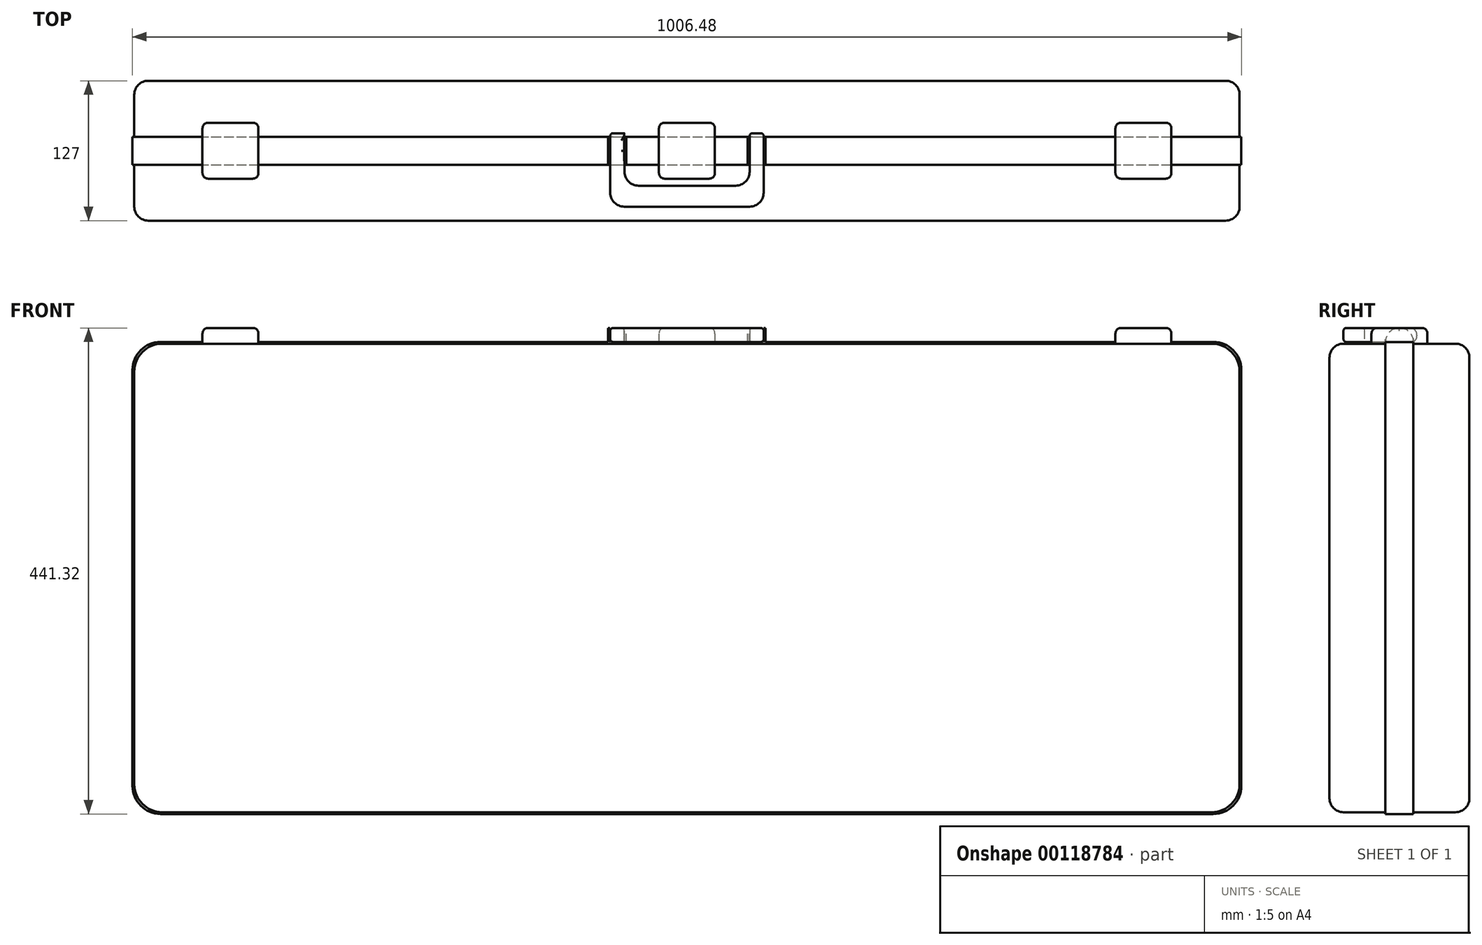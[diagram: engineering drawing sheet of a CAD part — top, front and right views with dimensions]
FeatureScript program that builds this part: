
annotation { "Feature Type Name" : "Feature", "Feature Type Description" : "" }
export const myFeature = defineFeature(function(context is Context, id is Id, definition is map)
    precondition{}
    {
        {
            var Q0;
            Q0=qCreatedBy(makeId("Front.planeOp"),FACE);
            var sketch = newSketch(context, id + "F0", { "sketchPlane" : qUnion([Q0])});
            skLineSegment(sketch, "E0.bottom", {"start": v(-501.65, 212.73) * mm, "end": v(501.65, 212.73) * mm});
            skLineSegment(sketch, "E0.top", {"start": v(-501.65, -212.73) * mm, "end": v(501.65, -212.73) * mm});
            skLineSegment(sketch, "E0.left", {"start": v(-501.65, 212.73) * mm, "end": v(-501.65, -212.73) * mm});
            skLineSegment(sketch, "E0.right", {"start": v(501.65, 212.73) * mm, "end": v(501.65, -212.73) * mm});
            skPoint(sketch, "E0.middle", {"position": v(0, 0) * mm});
            skSolve(sketch);
        }
        {
            var Q0;
            Q0 = qSketchRegion(id + "F0", true);
            extrude(context, id + "F1", {"entities" : qUnion([Q0]), "depth" : 63.5 * mm, "hasSecondDirection" : true, "secondDirectionOppositeDirection" : true, "secondDirectionDepth" : 63.5 * mm});
        }
        {
            var Q0;
            Q0=qCreatedBy(makeId("Front.planeOp"),FACE);
            var sketch = newSketch(context, id + "F2", { "sketchPlane" : qUnion([Q0])});
            skLineSegment(sketch, "E1.bottom", {"start": v(-503.24, 214.31) * mm, "end": v(503.24, 214.31) * mm});
            skLineSegment(sketch, "E1.top", {"start": v(-503.24, -214.31) * mm, "end": v(503.24, -214.31) * mm});
            skLineSegment(sketch, "E1.left", {"start": v(-503.24, 214.31) * mm, "end": v(-503.24, -214.31) * mm});
            skLineSegment(sketch, "E1.right", {"start": v(503.24, 214.31) * mm, "end": v(503.24, -214.31) * mm});
            skPoint(sketch, "E1.middle", {"position": v(0, 0) * mm});
            skSolve(sketch);
        }
        {
            var Q0;
            Q0 = qSketchRegion(id + "F2", true);
            extrude(context, id + "F3", {"entities" : qUnion([Q0]), "operationType" : NewBodyOperationType.ADD, "depth" : 12.7 * mm, "hasSecondDirection" : true, "secondDirectionOppositeDirection" : true, "secondDirectionDepth" : 12.7 * mm});
        }
        {
            var Q0;
            {var subQ0=sQuery(id+"F0.wireOp",EDGE,"E0.bottom");var subQ1=sQuery(id+"F0.wireOp",EDGE,"E0.right");Q0=makeQuery(id+"F3.boolean.opBoolean","SPLIT",EDGE,{"disambiguationData":[TD([makeQuery(id+"F1.opExtrude","CAP_FACE",FACE,{"disambiguationData":[OSD([subQ0,sQuery(id+"F0.wireOp",EDGE,"E0.top"),sQuery(id+"F0.wireOp",EDGE,"E0.left"),subQ1])],"isStart":false})])],"derivedFrom":makeQuery(id+"F1.opExtrude","SWEPT_EDGE",EDGE,{"disambiguationData":[OSD([subQ0,subQ1])]})});}
            var Q1;
            {var subQ0=sQuery(id+"F0.wireOp",EDGE,"E0.bottom");var subQ1=sQuery(id+"F0.wireOp",EDGE,"E0.right");Q1=makeQuery(id+"F3.boolean.opBoolean","SPLIT",EDGE,{"disambiguationData":[TD([makeQuery(id+"F1.opExtrude","CAP_FACE",FACE,{"disambiguationData":[OSD([subQ0,sQuery(id+"F0.wireOp",EDGE,"E0.top"),sQuery(id+"F0.wireOp",EDGE,"E0.left"),subQ1])],"isStart":true})])],"derivedFrom":makeQuery(id+"F1.opExtrude","SWEPT_EDGE",EDGE,{"disambiguationData":[OSD([subQ0,subQ1])]})});}
            var Q2;
            Q2=makeQuery(id+"F3.opExtrude","SWEPT_EDGE",EDGE,{"disambiguationData":[OSD([sQuery(id+"F2.wireOp",EDGE,"E1.bottom"),sQuery(id+"F2.wireOp",EDGE,"E1.right")])]});
            var Q3;
            {var subQ0=sQuery(id+"F0.wireOp",EDGE,"E0.right");var subQ1=sQuery(id+"F0.wireOp",EDGE,"E0.top");Q3=makeQuery(id+"F3.boolean.opBoolean","SPLIT",EDGE,{"disambiguationData":[TD([makeQuery(id+"F1.opExtrude","CAP_FACE",FACE,{"disambiguationData":[OSD([sQuery(id+"F0.wireOp",EDGE,"E0.bottom"),subQ1,sQuery(id+"F0.wireOp",EDGE,"E0.left"),subQ0])],"isStart":false})])],"derivedFrom":makeQuery(id+"F1.opExtrude","SWEPT_EDGE",EDGE,{"disambiguationData":[OSD([subQ1,subQ0])]})});}
            var Q4;
            Q4=makeQuery(id+"F3.opExtrude","SWEPT_EDGE",EDGE,{"disambiguationData":[OSD([sQuery(id+"F2.wireOp",EDGE,"E1.top"),sQuery(id+"F2.wireOp",EDGE,"E1.right")])]});
            var Q5;
            {var subQ0=sQuery(id+"F0.wireOp",EDGE,"E0.right");var subQ1=sQuery(id+"F0.wireOp",EDGE,"E0.top");Q5=makeQuery(id+"F3.boolean.opBoolean","SPLIT",EDGE,{"disambiguationData":[TD([makeQuery(id+"F1.opExtrude","CAP_FACE",FACE,{"disambiguationData":[OSD([sQuery(id+"F0.wireOp",EDGE,"E0.bottom"),subQ1,sQuery(id+"F0.wireOp",EDGE,"E0.left"),subQ0])],"isStart":true})])],"derivedFrom":makeQuery(id+"F1.opExtrude","SWEPT_EDGE",EDGE,{"disambiguationData":[OSD([subQ1,subQ0])]})});}
            var Q6;
            Q6=makeQuery(id+"F3.opExtrude","SWEPT_EDGE",EDGE,{"disambiguationData":[OSD([sQuery(id+"F2.wireOp",EDGE,"E1.bottom"),sQuery(id+"F2.wireOp",EDGE,"E1.left")])]});
            var Q7;
            {var subQ0=sQuery(id+"F0.wireOp",EDGE,"E0.bottom");var subQ1=sQuery(id+"F0.wireOp",EDGE,"E0.left");Q7=makeQuery(id+"F3.boolean.opBoolean","SPLIT",EDGE,{"disambiguationData":[TD([makeQuery(id+"F1.opExtrude","CAP_FACE",FACE,{"disambiguationData":[OSD([subQ0,sQuery(id+"F0.wireOp",EDGE,"E0.top"),subQ1,sQuery(id+"F0.wireOp",EDGE,"E0.right")])],"isStart":false})])],"derivedFrom":makeQuery(id+"F1.opExtrude","SWEPT_EDGE",EDGE,{"disambiguationData":[OSD([subQ0,subQ1])]})});}
            var Q8;
            {var subQ0=sQuery(id+"F0.wireOp",EDGE,"E0.bottom");var subQ1=sQuery(id+"F0.wireOp",EDGE,"E0.left");Q8=makeQuery(id+"F3.boolean.opBoolean","SPLIT",EDGE,{"disambiguationData":[TD([makeQuery(id+"F1.opExtrude","CAP_FACE",FACE,{"disambiguationData":[OSD([subQ0,sQuery(id+"F0.wireOp",EDGE,"E0.top"),subQ1,sQuery(id+"F0.wireOp",EDGE,"E0.right")])],"isStart":true})])],"derivedFrom":makeQuery(id+"F1.opExtrude","SWEPT_EDGE",EDGE,{"disambiguationData":[OSD([subQ0,subQ1])]})});}
            var Q9;
            {var subQ0=sQuery(id+"F0.wireOp",EDGE,"E0.left");var subQ1=sQuery(id+"F0.wireOp",EDGE,"E0.top");Q9=makeQuery(id+"F3.boolean.opBoolean","SPLIT",EDGE,{"disambiguationData":[TD([makeQuery(id+"F1.opExtrude","CAP_FACE",FACE,{"disambiguationData":[OSD([sQuery(id+"F0.wireOp",EDGE,"E0.bottom"),subQ1,subQ0,sQuery(id+"F0.wireOp",EDGE,"E0.right")])],"isStart":false})])],"derivedFrom":makeQuery(id+"F1.opExtrude","SWEPT_EDGE",EDGE,{"disambiguationData":[OSD([subQ1,subQ0])]})});}
            var Q10;
            Q10=makeQuery(id+"F3.opExtrude","SWEPT_EDGE",EDGE,{"disambiguationData":[OSD([sQuery(id+"F2.wireOp",EDGE,"E1.top"),sQuery(id+"F2.wireOp",EDGE,"E1.left")])]});
            var Q11;
            {var subQ0=sQuery(id+"F0.wireOp",EDGE,"E0.left");var subQ1=sQuery(id+"F0.wireOp",EDGE,"E0.top");Q11=makeQuery(id+"F3.boolean.opBoolean","SPLIT",EDGE,{"disambiguationData":[TD([makeQuery(id+"F1.opExtrude","CAP_FACE",FACE,{"disambiguationData":[OSD([sQuery(id+"F0.wireOp",EDGE,"E0.bottom"),subQ1,subQ0,sQuery(id+"F0.wireOp",EDGE,"E0.right")])],"isStart":true})])],"derivedFrom":makeQuery(id+"F1.opExtrude","SWEPT_EDGE",EDGE,{"disambiguationData":[OSD([subQ1,subQ0])]})});}
            fillet(context, id + "F4", {"entities" : qUnion([Q0, Q1, Q2, Q3, Q4, Q5, Q6, Q7, Q8, Q9, Q10, Q11]), "radius" : 25.4 * mm, "tangentPropagation" : true, "allowEdgeOverflow" : false});
        }
        {
            var Q0;
            Q0=makeQuery(id+"F1.opExtrude","CAP_EDGE",EDGE,{"disambiguationData":[OSD([sQuery(id+"F0.wireOp",EDGE,"E0.bottom")])],"isStart":false});
            var Q1;
            Q1=makeQuery(id+"F1.opExtrude","CAP_EDGE",EDGE,{"disambiguationData":[OSD([sQuery(id+"F0.wireOp",EDGE,"E0.bottom")])],"isStart":true});
            fillet(context, id + "F5", {"entities" : qUnion([Q0, Q1]), "radius" : 12.7 * mm, "tangentPropagation" : true, "allowEdgeOverflow" : false});
        }
        {
            var Q0;
            Q0=makeQuery(id+"F3.opExtrude","SWEPT_FACE",FACE,{"disambiguationData":[OSD([sQuery(id+"F2.wireOp",EDGE,"E1.bottom")])]});
            var sketch = newSketch(context, id + "F6", { "sketchPlane" : qUnion([Q0])});
            skLineSegment(sketch, "E2", {"start": v(-477.84, 12.7) * mm, "end": v(-439.74, 12.7) * mm, "construction": true});
            skLineSegment(sketch, "E3", {"start": v(-439.74, 12.7) * mm, "end": v(-439.74, 0) * mm, "construction": true});
            skLineSegment(sketch, "E4", {"start": v(-439.74, 12.7) * mm, "end": v(-439.74, 25.4) * mm, "construction": true});
            skLineSegment(sketch, "E5.bottom", {"start": v(-439.74, 25.4) * mm, "end": v(-388.94, 25.4) * mm});
            skLineSegment(sketch, "E5.top", {"start": v(-439.74, -25.4) * mm, "end": v(-388.94, -25.4) * mm});
            skLineSegment(sketch, "E5.left", {"start": v(-439.74, 25.4) * mm, "end": v(-439.74, -25.4) * mm});
            skLineSegment(sketch, "E5.right", {"start": v(-388.94, 25.4) * mm, "end": v(-388.94, -25.4) * mm});
            skLineSegment(sketch, "E6", {"start": v(477.84, 0) * mm, "end": v(439.74, 0) * mm, "construction": true});
            skLineSegment(sketch, "E7", {"start": v(439.74, 0) * mm, "end": v(439.74, 25.4) * mm, "construction": true});
            skLineSegment(sketch, "E8.bottom", {"start": v(439.74, 25.4) * mm, "end": v(388.94, 25.4) * mm});
            skLineSegment(sketch, "E8.top", {"start": v(439.74, -25.4) * mm, "end": v(388.94, -25.4) * mm});
            skLineSegment(sketch, "E8.left", {"start": v(439.74, 25.4) * mm, "end": v(439.74, -25.4) * mm});
            skLineSegment(sketch, "E8.right", {"start": v(388.94, 25.4) * mm, "end": v(388.94, -25.4) * mm});
            skLineSegment(sketch, "E9.bottom", {"start": v(25.4, -25.4) * mm, "end": v(-25.4, -25.4) * mm});
            skLineSegment(sketch, "E9.top", {"start": v(25.4, 25.4) * mm, "end": v(-25.4, 25.4) * mm});
            skLineSegment(sketch, "E9.left", {"start": v(25.4, -25.4) * mm, "end": v(25.4, 25.4) * mm});
            skLineSegment(sketch, "E9.right", {"start": v(-25.4, -25.4) * mm, "end": v(-25.4, 25.4) * mm});
            skPoint(sketch, "E9.middle", {"position": v(0, 0) * mm});
            skSolve(sketch);
        }
        {
            var Q0;
            Q0 = qSketchRegion(id + "F6", true);
            extrude(context, id + "F7", {"entities" : qUnion([Q0]), "operationType" : NewBodyOperationType.ADD, "depth" : 12.7 * mm, "hasSecondDirection" : true, "secondDirectionOppositeDirection" : true, "secondDirectionDepth" : 25.4 * mm});
        }
        {
            var Q0;
            Q0=makeQuery(id+"F7.opExtrude","SWEPT_EDGE",EDGE,{"disambiguationData":[OSD([sQuery(id+"F6.wireOp",EDGE,"E9.bottom"),sQuery(id+"F6.wireOp",EDGE,"E9.left")])]});
            var Q1;
            Q1=makeQuery(id+"F7.opExtrude","SWEPT_EDGE",EDGE,{"disambiguationData":[OSD([sQuery(id+"F6.wireOp",EDGE,"E9.bottom"),sQuery(id+"F6.wireOp",EDGE,"E9.right")])]});
            var Q2;
            Q2=makeQuery(id+"F7.opExtrude","SWEPT_EDGE",EDGE,{"disambiguationData":[OSD([sQuery(id+"F6.wireOp",EDGE,"E9.top"),sQuery(id+"F6.wireOp",EDGE,"E9.right")])]});
            var Q3;
            Q3=makeQuery(id+"F7.opExtrude","SWEPT_EDGE",EDGE,{"disambiguationData":[OSD([sQuery(id+"F6.wireOp",EDGE,"E9.top"),sQuery(id+"F6.wireOp",EDGE,"E9.left")])]});
            var Q4;
            Q4=makeQuery(id+"F7.opExtrude","SWEPT_EDGE",EDGE,{"disambiguationData":[OSD([sQuery(id+"F6.wireOp",EDGE,"E5.bottom"),sQuery(id+"F6.wireOp",EDGE,"E5.right")])]});
            var Q5;
            Q5=makeQuery(id+"F7.opExtrude","SWEPT_EDGE",EDGE,{"disambiguationData":[OSD([sQuery(id+"F6.wireOp",EDGE,"E5.bottom"),sQuery(id+"F6.wireOp",EDGE,"E5.left")])]});
            var Q6;
            Q6=makeQuery(id+"F7.opExtrude","SWEPT_EDGE",EDGE,{"disambiguationData":[OSD([sQuery(id+"F6.wireOp",EDGE,"E5.top"),sQuery(id+"F6.wireOp",EDGE,"E5.right")])]});
            var Q7;
            Q7=makeQuery(id+"F7.opExtrude","SWEPT_EDGE",EDGE,{"disambiguationData":[OSD([sQuery(id+"F6.wireOp",EDGE,"E5.top"),sQuery(id+"F6.wireOp",EDGE,"E5.left")])]});
            var Q8;
            Q8=makeQuery(id+"F7.opExtrude","SWEPT_EDGE",EDGE,{"disambiguationData":[OSD([sQuery(id+"F6.wireOp",EDGE,"E8.top"),sQuery(id+"F6.wireOp",EDGE,"E8.left")])]});
            var Q9;
            Q9=makeQuery(id+"F7.opExtrude","SWEPT_EDGE",EDGE,{"disambiguationData":[OSD([sQuery(id+"F6.wireOp",EDGE,"E8.top"),sQuery(id+"F6.wireOp",EDGE,"E8.right")])]});
            var Q10;
            Q10=makeQuery(id+"F7.opExtrude","SWEPT_EDGE",EDGE,{"disambiguationData":[OSD([sQuery(id+"F6.wireOp",EDGE,"E8.bottom"),sQuery(id+"F6.wireOp",EDGE,"E8.right")])]});
            var Q11;
            Q11=makeQuery(id+"F7.opExtrude","SWEPT_EDGE",EDGE,{"disambiguationData":[OSD([sQuery(id+"F6.wireOp",EDGE,"E8.bottom"),sQuery(id+"F6.wireOp",EDGE,"E8.left")])]});
            var Q12;
            Q12=makeQuery(id+"F7.opExtrude","CAP_FACE",FACE,{"disambiguationData":[OSD([sQuery(id+"F6.wireOp",EDGE,"E9.bottom"),sQuery(id+"F6.wireOp",EDGE,"E9.top"),sQuery(id+"F6.wireOp",EDGE,"E9.left"),sQuery(id+"F6.wireOp",EDGE,"E9.right")])],"isStart":false});
            var Q13;
            Q13=makeQuery(id+"F7.opExtrude","CAP_FACE",FACE,{"disambiguationData":[OSD([sQuery(id+"F6.wireOp",EDGE,"E8.bottom"),sQuery(id+"F6.wireOp",EDGE,"E8.top"),sQuery(id+"F6.wireOp",EDGE,"E8.left"),sQuery(id+"F6.wireOp",EDGE,"E8.right")])],"isStart":false});
            var Q14;
            Q14=makeQuery(id+"F7.opExtrude","CAP_EDGE",EDGE,{"disambiguationData":[OSD([sQuery(id+"F6.wireOp",EDGE,"E5.left")])],"isStart":false});
            var Q15;
            Q15=makeQuery(id+"F7.opExtrude","CAP_FACE",FACE,{"disambiguationData":[OSD([sQuery(id+"F6.wireOp",EDGE,"E5.bottom"),sQuery(id+"F6.wireOp",EDGE,"E5.top"),sQuery(id+"F6.wireOp",EDGE,"E5.left"),sQuery(id+"F6.wireOp",EDGE,"E5.right")])],"isStart":false});
            fillet(context, id + "F8", {"entities" : qUnion([Q0, Q1, Q2, Q3, Q4, Q5, Q6, Q7, Q8, Q9, Q10, Q11, Q12, Q13, Q14, Q15]), "radius" : 5.08 * mm, "tangentPropagation" : true, "allowEdgeOverflow" : false});
        }
        {
            var Q0;
            {var subQ3=sQuery(id+"F2.wireOp",EDGE,"E1.bottom");Q0=makeQuery(id+"F7.boolean.opBoolean","SPLIT",FACE,{"disambiguationData":[TD([makeQuery(id+"F7.opExtrude","SWEPT_FACE",FACE,{"disambiguationData":[OSD([sQuery(id+"F6.wireOp",EDGE,"E5.right")])]})])],"derivedFrom":makeQuery(id+"F3.opExtrude","SWEPT_FACE",FACE,{"disambiguationData":[OSD([subQ3])]})});}
            var sketch = newSketch(context, id + "F9", { "sketchPlane" : qUnion([Q0])});
            skLineSegment(sketch, "E10", {"start": v(0, 0) * mm, "end": v(-69.85, 0) * mm, "construction": true});
            skLineSegment(sketch, "E11", {"start": v(0, 0) * mm, "end": v(69.85, 0) * mm, "construction": true});
            skLineSegment(sketch, "E12", {"start": v(-69.85, 0) * mm, "end": v(-69.85, 12.7) * mm, "construction": true});
            skLineSegment(sketch, "E13", {"start": v(-69.85, 12.7) * mm, "end": v(-69.85, -12.7) * mm});
            skLineSegment(sketch, "E14", {"start": v(-69.85, -12.7) * mm, "end": v(-71.44, -12.7) * mm});
            skLineSegment(sketch, "E15", {"start": v(-71.44, -12.7) * mm, "end": v(-71.44, 12.7) * mm});
            skLineSegment(sketch, "E16", {"start": v(-71.44, 12.7) * mm, "end": v(-69.85, 12.7) * mm});
            skLineSegment(sketch, "E17", {"start": v(-69.85, 0) * mm, "end": v(-69.6, 0) * mm});
            skLineSegment(sketch, "E18", {"start": v(-69.6, 0) * mm, "end": v(-56.9, 0) * mm, "construction": true});
            skLineSegment(sketch, "E19", {"start": v(-56.9, 0) * mm, "end": v(-56.64, 0) * mm, "construction": true});
            skLineSegment(sketch, "E20", {"start": v(-56.64, 0) * mm, "end": v(-56.64, 12.7) * mm, "construction": true});
            skLineSegment(sketch, "E21.bottom", {"start": v(-56.64, 12.7) * mm, "end": v(-55.05, 12.7) * mm});
            skLineSegment(sketch, "E21.top", {"start": v(-56.64, -12.7) * mm, "end": v(-55.05, -12.7) * mm});
            skLineSegment(sketch, "E21.left", {"start": v(-56.64, 12.7) * mm, "end": v(-56.64, -12.7) * mm});
            skLineSegment(sketch, "E21.right", {"start": v(-55.05, 12.7) * mm, "end": v(-55.05, -12.7) * mm});
            skLineSegment(sketch, "E22", {"start": v(-69.6, 0) * mm, "end": v(-69.6, -50.8) * mm});
            skLineSegment(sketch, "E23", {"start": v(-56.9, 0) * mm, "end": v(-56.64, -31.75) * mm});
            skLineSegment(sketch, "E24", {"start": v(69.85, 0) * mm, "end": v(69.85, 12.7) * mm, "construction": true});
            skLineSegment(sketch, "E25.bottom", {"start": v(69.85, 12.7) * mm, "end": v(71.44, 12.7) * mm});
            skLineSegment(sketch, "E25.top", {"start": v(69.85, -12.7) * mm, "end": v(71.44, -12.7) * mm});
            skLineSegment(sketch, "E25.left", {"start": v(69.85, 12.7) * mm, "end": v(69.85, -12.7) * mm});
            skLineSegment(sketch, "E25.right", {"start": v(71.44, 12.7) * mm, "end": v(71.44, -12.7) * mm});
            skLineSegment(sketch, "E26", {"start": v(69.85, 0) * mm, "end": v(69.6, 0) * mm, "construction": true});
            skLineSegment(sketch, "E27", {"start": v(69.6, 0) * mm, "end": v(56.9, 0) * mm, "construction": true});
            skLineSegment(sketch, "E28", {"start": v(56.9, 0) * mm, "end": v(56.64, 0) * mm, "construction": true});
            skLineSegment(sketch, "E29", {"start": v(56.64, 0) * mm, "end": v(56.64, 12.7) * mm, "construction": true});
            skLineSegment(sketch, "E30.bottom", {"start": v(56.64, 12.7) * mm, "end": v(55.05, 12.7) * mm});
            skLineSegment(sketch, "E30.top", {"start": v(56.64, -12.7) * mm, "end": v(55.05, -12.7) * mm});
            skLineSegment(sketch, "E30.left", {"start": v(56.64, 12.7) * mm, "end": v(56.64, -12.7) * mm});
            skLineSegment(sketch, "E30.right", {"start": v(55.05, 12.7) * mm, "end": v(55.05, -12.7) * mm});
            skLineSegment(sketch, "E31", {"start": v(56.9, 0) * mm, "end": v(56.9, -31.75) * mm});
            skLineSegment(sketch, "E32", {"start": v(69.6, 0) * mm, "end": v(69.6, -50.8) * mm});
            skLineSegment(sketch, "E33", {"start": v(56.9, -31.75) * mm, "end": v(-56.64, -31.75) * mm});
            skLineSegment(sketch, "E34", {"start": v(69.6, -50.8) * mm, "end": v(-69.6, -50.8) * mm});
            skLineSegment(sketch, "E35", {"start": v(-69.6, 0) * mm, "end": v(-69.6, 15.88) * mm});
            skLineSegment(sketch, "E36", {"start": v(-69.6, 15.88) * mm, "end": v(-56.9, 15.88) * mm});
            skLineSegment(sketch, "E37", {"start": v(-56.9, 15.88) * mm, "end": v(-56.9, 0) * mm});
            skLineSegment(sketch, "E38", {"start": v(56.9, 0) * mm, "end": v(56.9, 15.88) * mm});
            skLineSegment(sketch, "E39", {"start": v(56.9, 15.88) * mm, "end": v(69.6, 15.88) * mm});
            skLineSegment(sketch, "E40", {"start": v(69.6, 15.88) * mm, "end": v(69.6, 0) * mm});
            skSolve(sketch);
        }
        {
            var Q0;
            Q0 = qSketchRegion(id + "F9", true);
            extrude(context, id + "F10", {"entities" : qUnion([Q0]), "operationType" : NewBodyOperationType.ADD, "depth" : 12.7 * mm});
        }
        {
            var Q0;
            Q0=makeQuery(id+"F10.opExtrude","CAP_EDGE",EDGE,{"disambiguationData":[OSD([sQuery(id+"F9.wireOp",EDGE,"E14")])],"isStart":false});
            var Q1;
            Q1=makeQuery(id+"F10.opExtrude","CAP_EDGE",EDGE,{"disambiguationData":[OSD([sQuery(id+"F9.wireOp",EDGE,"E16")])],"isStart":false});
            var Q2;
            Q2=makeQuery(id+"F10.opExtrude","CAP_EDGE",EDGE,{"disambiguationData":[OSD([sQuery(id+"F9.wireOp",EDGE,"E21.top")])],"isStart":false});
            var Q3;
            Q3=makeQuery(id+"F10.opExtrude","CAP_EDGE",EDGE,{"disambiguationData":[OSD([sQuery(id+"F9.wireOp",EDGE,"E21.bottom")])],"isStart":false});
            var Q4;
            Q4=makeQuery(id+"F10.opExtrude","CAP_EDGE",EDGE,{"disambiguationData":[OSD([sQuery(id+"F9.wireOp",EDGE,"E30.top")])],"isStart":false});
            var Q5;
            Q5=makeQuery(id+"F10.opExtrude","CAP_EDGE",EDGE,{"disambiguationData":[OSD([sQuery(id+"F9.wireOp",EDGE,"E30.bottom")])],"isStart":false});
            var Q6;
            Q6=makeQuery(id+"F10.opExtrude","CAP_EDGE",EDGE,{"disambiguationData":[OSD([sQuery(id+"F9.wireOp",EDGE,"E25.bottom")])],"isStart":false});
            var Q7;
            Q7=makeQuery(id+"F10.opExtrude","CAP_EDGE",EDGE,{"disambiguationData":[OSD([sQuery(id+"F9.wireOp",EDGE,"E25.top")])],"isStart":false});
            fillet(context, id + "F11", {"entities" : qUnion([Q0, Q1, Q2, Q3, Q4, Q5, Q6, Q7]), "radius" : 12.7 * mm, "tangentPropagation" : true, "allowEdgeOverflow" : false});
        }
        {
            var Q0;
            Q0=makeQuery(id+"F10.opExtrude","CAP_EDGE",EDGE,{"disambiguationData":[OSD([sQuery(id+"F9.wireOp",EDGE,"E39")])],"isStart":false});
            var Q1;
            Q1=makeQuery(id+"F10.opExtrude","CAP_EDGE",EDGE,{"disambiguationData":[OSD([sQuery(id+"F9.wireOp",EDGE,"E39")])],"isStart":true});
            var Q2;
            Q2=makeQuery(id+"F10.opExtrude","CAP_EDGE",EDGE,{"disambiguationData":[OSD([sQuery(id+"F9.wireOp",EDGE,"E36")])],"isStart":false});
            var Q3;
            Q3=makeQuery(id+"F10.opExtrude","CAP_EDGE",EDGE,{"disambiguationData":[OSD([sQuery(id+"F9.wireOp",EDGE,"E36")])],"isStart":true});
            fillet(context, id + "F12", {"entities" : qUnion([Q0, Q1, Q2, Q3]), "radius" : 6.35 * mm, "tangentPropagation" : true, "allowEdgeOverflow" : false});
        }
        {
            var Q0;
            Q0=makeQuery(id+"F10.opExtrude","SWEPT_EDGE",EDGE,{"disambiguationData":[OSD([sQuery(id+"F9.wireOp",EDGE,"E23"),sQuery(id+"F9.wireOp",EDGE,"E33")])]});
            var Q1;
            Q1=makeQuery(id+"F10.opExtrude","SWEPT_EDGE",EDGE,{"disambiguationData":[OSD([sQuery(id+"F9.wireOp",EDGE,"E22"),sQuery(id+"F9.wireOp",EDGE,"E34")])]});
            var Q2;
            Q2=makeQuery(id+"F10.opExtrude","SWEPT_EDGE",EDGE,{"disambiguationData":[OSD([sQuery(id+"F9.wireOp",EDGE,"E31"),sQuery(id+"F9.wireOp",EDGE,"E33")])]});
            var Q3;
            Q3=makeQuery(id+"F10.opExtrude","SWEPT_EDGE",EDGE,{"disambiguationData":[OSD([sQuery(id+"F9.wireOp",EDGE,"E32"),sQuery(id+"F9.wireOp",EDGE,"E34")])]});
            fillet(context, id + "F13", {"entities" : qUnion([Q0, Q1, Q2, Q3]), "radius" : 12.7 * mm, "tangentPropagation" : true, "allowEdgeOverflow" : false});
        }
        {
            var Q0;
            {var subQ0=sQuery(id+"F9.wireOp",EDGE,"E33");var subQ1=sQuery(id+"F9.wireOp",EDGE,"E23");Q0=makeQuery(id+"F13.opFillet","BLEND_EDGE",EDGE,{"blendedFrom":[makeQuery(id+"F10.opExtrude","SWEPT_EDGE",EDGE,{"disambiguationData":[OSD([subQ1,subQ0])]}),makeQuery(id+"F10.opExtrude","CAP_FACE",FACE,{"disambiguationData":[OSD([sQuery(id+"F9.wireOp",EDGE,"E22"),subQ1,sQuery(id+"F9.wireOp",EDGE,"E31"),sQuery(id+"F9.wireOp",EDGE,"E32"),subQ0,sQuery(id+"F9.wireOp",EDGE,"E34"),sQuery(id+"F9.wireOp",EDGE,"E35"),sQuery(id+"F9.wireOp",EDGE,"E36"),sQuery(id+"F9.wireOp",EDGE,"E37"),sQuery(id+"F9.wireOp",EDGE,"E38"),sQuery(id+"F9.wireOp",EDGE,"E39"),sQuery(id+"F9.wireOp",EDGE,"E40")])],"isStart":false})],"blendedInto":[makeQuery(id+"F10.opExtrude","CAP_FACE",FACE,{"disambiguationData":[OSD([sQuery(id+"F9.wireOp",EDGE,"E22"),subQ1,sQuery(id+"F9.wireOp",EDGE,"E31"),sQuery(id+"F9.wireOp",EDGE,"E32"),subQ0,sQuery(id+"F9.wireOp",EDGE,"E34"),sQuery(id+"F9.wireOp",EDGE,"E35"),sQuery(id+"F9.wireOp",EDGE,"E36"),sQuery(id+"F9.wireOp",EDGE,"E37"),sQuery(id+"F9.wireOp",EDGE,"E38"),sQuery(id+"F9.wireOp",EDGE,"E39"),sQuery(id+"F9.wireOp",EDGE,"E40")])],"isStart":false})]});}
            var Q1;
            {var subQ0=sQuery(id+"F9.wireOp",EDGE,"E34");var subQ1=sQuery(id+"F9.wireOp",EDGE,"E22");Q1=makeQuery(id+"F13.opFillet","BLEND_EDGE",EDGE,{"blendedFrom":[makeQuery(id+"F10.opExtrude","SWEPT_EDGE",EDGE,{"disambiguationData":[OSD([subQ1,subQ0])]}),makeQuery(id+"F10.opExtrude","CAP_FACE",FACE,{"disambiguationData":[OSD([subQ1,sQuery(id+"F9.wireOp",EDGE,"E23"),sQuery(id+"F9.wireOp",EDGE,"E31"),sQuery(id+"F9.wireOp",EDGE,"E32"),sQuery(id+"F9.wireOp",EDGE,"E33"),subQ0,sQuery(id+"F9.wireOp",EDGE,"E35"),sQuery(id+"F9.wireOp",EDGE,"E36"),sQuery(id+"F9.wireOp",EDGE,"E37"),sQuery(id+"F9.wireOp",EDGE,"E38"),sQuery(id+"F9.wireOp",EDGE,"E39"),sQuery(id+"F9.wireOp",EDGE,"E40")])],"isStart":false})],"blendedInto":[makeQuery(id+"F10.opExtrude","CAP_FACE",FACE,{"disambiguationData":[OSD([subQ1,sQuery(id+"F9.wireOp",EDGE,"E23"),sQuery(id+"F9.wireOp",EDGE,"E31"),sQuery(id+"F9.wireOp",EDGE,"E32"),sQuery(id+"F9.wireOp",EDGE,"E33"),subQ0,sQuery(id+"F9.wireOp",EDGE,"E35"),sQuery(id+"F9.wireOp",EDGE,"E36"),sQuery(id+"F9.wireOp",EDGE,"E37"),sQuery(id+"F9.wireOp",EDGE,"E38"),sQuery(id+"F9.wireOp",EDGE,"E39"),sQuery(id+"F9.wireOp",EDGE,"E40")])],"isStart":false})]});}
            var Q2;
            {var subQ0=sQuery(id+"F9.wireOp",EDGE,"E40");var subQ1=sQuery(id+"F9.wireOp",EDGE,"E32");var subQ3=sQuery(id+"F9.wireOp",EDGE,"E23");var subQ4=sQuery(id+"F9.wireOp",EDGE,"E35");var subQ5=sQuery(id+"F9.wireOp",EDGE,"E22");var subQ6=sQuery(id+"F9.wireOp",EDGE,"E38");var subQ7=sQuery(id+"F9.wireOp",EDGE,"E31");var subQ8=sQuery(id+"F9.wireOp",EDGE,"E33");var subQ9=sQuery(id+"F9.wireOp",EDGE,"E34");Q2=makeQuery(id+"F13.opFillet","BLEND_EDGE",EDGE,{"blendedFrom":[makeQuery(id+"F10.opExtrude","SWEPT_EDGE",EDGE,{"disambiguationData":[OSD([subQ1,subQ9])]}),makeQuery(id+"F10.boolean.opBoolean","SPLIT",FACE,{"disambiguationData":[TD([makeQuery(id+"F10.opExtrude","SWEPT_FACE",FACE,{"disambiguationData":[OSD([sQuery(id+"F9.wireOp",EDGE,"E14")])]})])],"derivedFrom":makeQuery(id+"F10.opExtrude","CAP_FACE",FACE,{"disambiguationData":[OSD([subQ5,subQ3,subQ7,subQ1,subQ8,subQ9,subQ4,sQuery(id+"F9.wireOp",EDGE,"E36"),sQuery(id+"F9.wireOp",EDGE,"E37"),subQ6,sQuery(id+"F9.wireOp",EDGE,"E39"),subQ0])],"isStart":true})})],"blendedInto":[makeQuery(id+"F10.boolean.opBoolean","SPLIT",FACE,{"disambiguationData":[TD([makeQuery(id+"F10.opExtrude","SWEPT_FACE",FACE,{"disambiguationData":[OSD([sQuery(id+"F9.wireOp",EDGE,"E14")])]})])],"derivedFrom":makeQuery(id+"F10.opExtrude","CAP_FACE",FACE,{"disambiguationData":[OSD([subQ5,subQ3,subQ7,subQ1,subQ8,subQ9,subQ4,sQuery(id+"F9.wireOp",EDGE,"E36"),sQuery(id+"F9.wireOp",EDGE,"E37"),subQ6,sQuery(id+"F9.wireOp",EDGE,"E39"),subQ0])],"isStart":true})})]});}
            fillet(context, id + "F14", {"entities" : qUnion([Q0, Q1, Q2]), "radius" : 2.54 * mm, "tangentPropagation" : true, "allowEdgeOverflow" : false});
        }
    });
